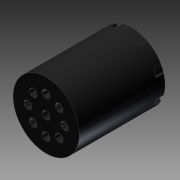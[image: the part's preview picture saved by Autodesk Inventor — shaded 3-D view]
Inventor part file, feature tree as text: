
AUTODESK INVENTOR PART (.ipt)
format: ipt  version: 2012 (Build 160160000, 160)  size: 697,344 bytes
history: native  units: mm
features: extrude x6, sketch x6, pattern_circular x3, other x1, helix x1, mirror x1
ambient origin geometry x8: Origin, YZ Plane, XZ Plane, XY Plane, X Axis, Y Axis, Z Axis, Center Point
bodies: Solid1 (feature_tree)
feature tree (18):
  extrude  "Extrusion1"  Depth=54.0mm
  extrude  "Extrusion2"  Depth=6.2mm
  sketch  "Sketch4"  dims[d15=100.0mm d16=0.0mm d17=15.0mm]
  other  "Work Axis1"
  helix  "Coil1"  [1 undecoded]
  pattern_circular  "Circular Pattern1"  Count=8 Angle=360.0deg
  sketch  "Sketch12"  dims[d18=1.0mm d19=2.9mm]
  extrude  "Extrusion10"  Depth=15.0mm
  extrude  "Extrusion11"  Depth=2.9mm
  extrude  "Extrusion12"  Depth=5.588mm
  mirror  "Mirror2"
  pattern_circular  "Circular Pattern4"  Count=10 Angle=360.0deg
  extrude  "Extrusion13"  Depth=7.5mm
  pattern_circular  "Circular Pattern5"  Count=8 Angle=360.0deg
  sketch  "Sketch2"  dims[d0=6.4mm d4=54.0mm]
  sketch  "Sketch3"  dims[d5=34.0mm d6=36.0mm d7=0.0mm d8=0.0mm d9=6.2mm d10=15.0mm d11=80.0mm d13=360.0deg]
  sketch  "Sketch14"  dims[d20=60.0mm d22=360.0deg d24=5.588mm]
  sketch  "Sketch15"  dims[d25=406.4mm d26=10.0mm d27=10.0mm d28=0.0mm d29=90.0deg d30=90.0deg d31=0.0mm d32=0.0mm d33=100.0mm d34=0.0mm d35=80.0mm d36=360.0deg d82=7.5mm d83=80.0mm d85=360.0deg d87=50.0mm d88=32.0mm d89=35.25mm d90=1.5mm d91=0.0mm d92=14.25mm d93=0.0mm d94=0.0mm d96=1.047198mm d103=22.5deg d104=1.047198mm d105=50.0mm d106=1.047198mm d107=6.0mm d108=0.0mm d109=80.0mm d110=360.0deg d112=17.625mm d113=14.25mm d114=7.24375mm d115=34.0mm d116=0.0mm d117=80.0mm d118=360.0deg]
note: 1 required parameter value undecoded (feature->parameter linkage not recoverable at this tier; creation-order binding heuristic only, values carry confidence <= 0.55)
